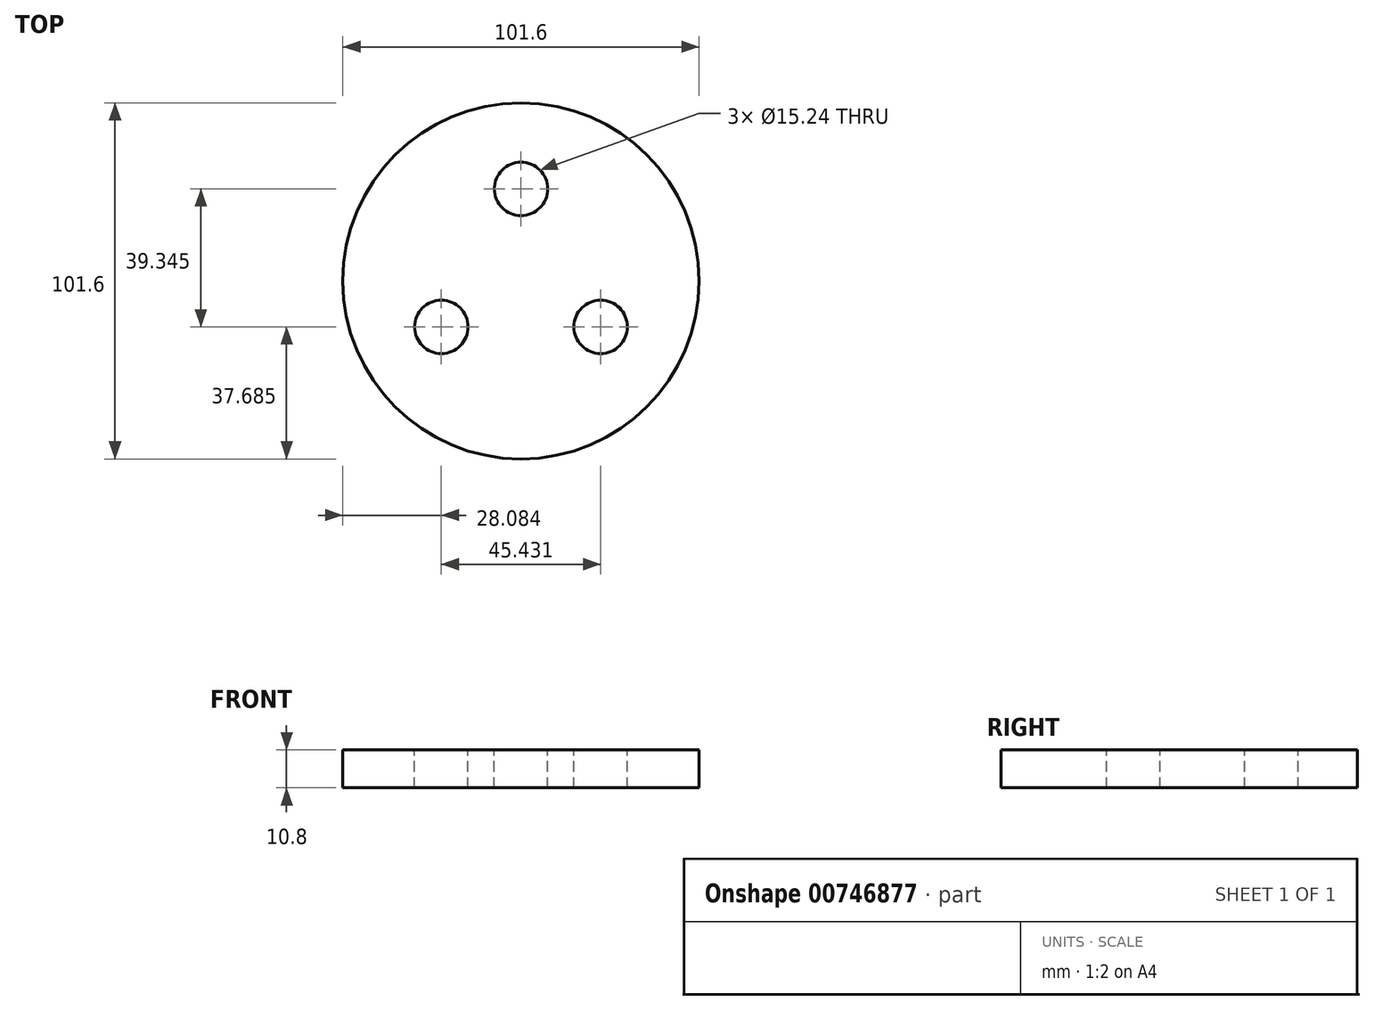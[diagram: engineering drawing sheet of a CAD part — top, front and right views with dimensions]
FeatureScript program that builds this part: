
annotation { "Feature Type Name" : "Feature", "Feature Type Description" : "" }
export const myFeature = defineFeature(function(context is Context, id is Id, definition is map)
    precondition{}
    {
        {
            var Q0;
            Q0=qCreatedBy(makeId("Top.planeOp"),FACE);
            var sketch = newSketch(context, id + "F0", { "sketchPlane" : qUnion([Q0])});
            skCircle(sketch, "E0", {"center": v(0, 0) * mm, "radius": 50.8 * mm});
            skSolve(sketch);
        }
        {
            var Q0;
            Q0=makeQuery(id+"F0.imprint","IMPRINT",FACE,{"disambiguationData":[TD([[makeQuery(id+"F0.imprint","IMPRINT",EDGE,{"derivedFrom":sQuery(id+"F0.wireOp",EDGE,"E0")}),1.0]])]});
            var Q1;
            Q1=sQuery(id+"F0.wireOp",EDGE,"E0");
            extrude(context, id + "F1", {"entities" : qUnion([Q0]), "surfaceEntities" : qUnion([Q1]), "depth" : 10.8 * mm, "offsetDistance" : 25.4 * mm});
        }
        {
            var Q0;
            Q0=makeQuery(id+"F1.opExtrude","CAP_FACE",FACE,{"disambiguationData":[OSD([sQuery(id+"F0.wireOp",EDGE,"E0")])],"isStart":false});
            var sketch = newSketch(context, id + "F2", { "sketchPlane" : qUnion([Q0])});
            skCircle(sketch, "E1", {"center": v(0, 26.23) * mm, "radius": 7.62 * mm});
            skCircle(sketch, "E2.1.0", {"center": v(-22.72, -13.11) * mm, "radius": 7.62 * mm});
            skCircle(sketch, "E2.2.0", {"center": v(22.72, -13.11) * mm, "radius": 7.62 * mm});
            skPoint(sketch, "E2.center", {"position": v(0, 0) * mm});
            skSolve(sketch);
        }
        {
            var Q0;
            Q0=makeQuery(id+"F2.imprint","IMPRINT",FACE,{"disambiguationData":[TD([[makeQuery(id+"F2.imprint","IMPRINT",EDGE,{"derivedFrom":sQuery(id+"F2.wireOp",EDGE,"E2.1.0")}),1.0]])]});
            var Q1;
            Q1=makeQuery(id+"F2.imprint","IMPRINT",FACE,{"disambiguationData":[TD([[makeQuery(id+"F2.imprint","IMPRINT",EDGE,{"derivedFrom":sQuery(id+"F2.wireOp",EDGE,"E1")}),1.0]])]});
            var Q2;
            Q2=makeQuery(id+"F2.imprint","IMPRINT",FACE,{"disambiguationData":[TD([[makeQuery(id+"F2.imprint","IMPRINT",EDGE,{"derivedFrom":sQuery(id+"F2.wireOp",EDGE,"E2.2.0")}),1.0]])]});
            extrude(context, id + "F3", {"entities" : qUnion([Q0, Q1, Q2]), "operationType" : NewBodyOperationType.REMOVE, "endBound" : BoundingType.THROUGH_ALL, "oppositeDirection" : true, "depth" : 25.4 * mm, "offsetDistance" : 25.4 * mm});
        }
    });
